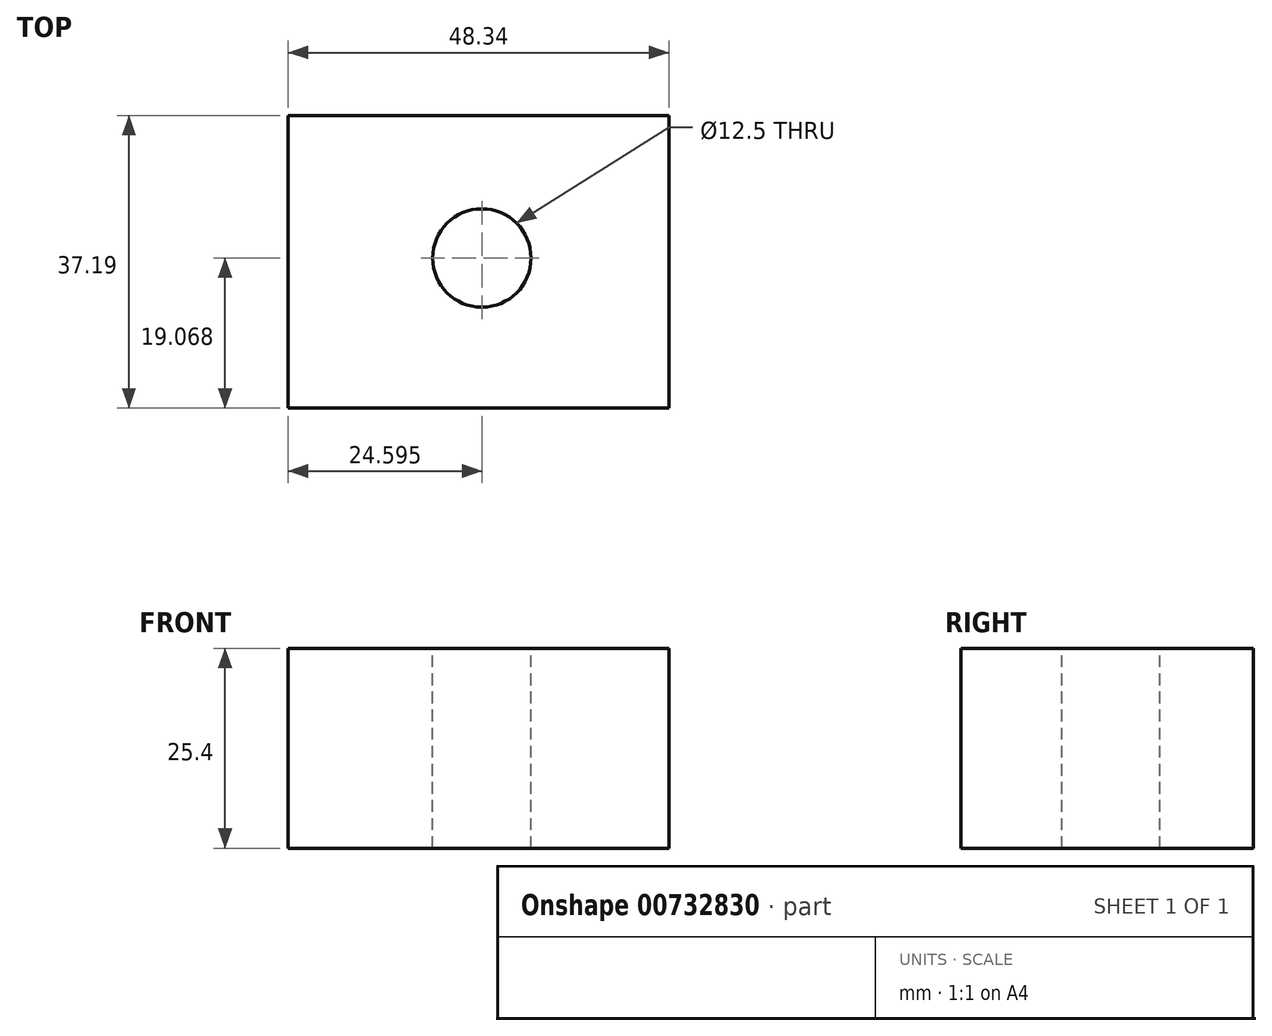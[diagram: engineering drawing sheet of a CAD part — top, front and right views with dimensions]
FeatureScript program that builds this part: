
annotation { "Feature Type Name" : "Feature", "Feature Type Description" : "" }
export const myFeature = defineFeature(function(context is Context, id is Id, definition is map)
    precondition{}
    {
        {
            var Q0;
            Q0=qCreatedBy(makeId("Top.planeOp"),FACE);
            var sketch = newSketch(context, id + "F0", { "sketchPlane" : qUnion([Q0])});
            skLineSegment(sketch, "E0.bottom", {"start": v(0, 0) * mm, "end": v(48.34, 0) * mm});
            skLineSegment(sketch, "E0.top", {"start": v(0, 37.19) * mm, "end": v(48.34, 37.19) * mm});
            skLineSegment(sketch, "E0.left", {"start": v(0, 0) * mm, "end": v(0, 37.19) * mm});
            skLineSegment(sketch, "E0.right", {"start": v(48.34, 0) * mm, "end": v(48.34, 37.19) * mm});
            skSolve(sketch);
        }
        {
            var Q0;
            Q0 = qSketchRegion(id + "F0", true);
            extrude(context, id + "F1", {"entities" : qUnion([Q0]), "depth" : 25.4 * mm, "offsetDistance" : 25.4 * mm});
        }
        {
            var Q0;
            Q0=makeQuery(id+"F1.opExtrude","CAP_FACE",FACE,{"disambiguationData":[OSD([sQuery(id+"F0.wireOp",EDGE,"E0.bottom"),sQuery(id+"F0.wireOp",EDGE,"E0.top"),sQuery(id+"F0.wireOp",EDGE,"E0.left"),sQuery(id+"F0.wireOp",EDGE,"E0.right")])],"isStart":false});
            var sketch = newSketch(context, id + "F2", { "sketchPlane" : qUnion([Q0])});
            skPoint(sketch, "E1", {"position": v(24.6, 19.07) * mm});
            skSolve(sketch);
        }
        {
            var Q0;
            Q0=sQuery(id+"F2.wireOp",VERTEX,"E1");
            var Q1;
            Q1=makeQuery(id+"F1.opExtrude","SWEPT_BODY",BODY,{"disambiguationData":[OSD([sQuery(id+"F0.wireOp",EDGE,"E0.bottom"),sQuery(id+"F0.wireOp",EDGE,"E0.top"),sQuery(id+"F0.wireOp",EDGE,"E0.left"),sQuery(id+"F0.wireOp",EDGE,"E0.right")])]});
            hole(context, id + "F3", {"style" : HoleStyle.SIMPLE, "endStyle" : HoleEndStyle.THROUGH, "standardTappedOrClearance" : lookupTablePath({ "standard" : "ISO", "engagement" : "75%", "pitch" : "1.5 mm", "size" : "M14", "type" : "Tapped" }), "standardBlindInLast" : lookupTablePath({ "standard" : "ISO", "engagement" : "75%", "pitch" : "1.5 mm", "size" : "M14", "type" : "Tapped" }), "holeDiameter" : 12.5 * mm, "majorDiameter" : 14 * mm, "showTappedDepth" : true, "isTappedThrough" : true, "tappedDepth" : 12.7 * mm, "tapClearance" : 3, "startFromSketch" : true, "locations" : qUnion([Q0]), "scope" : qUnion([Q1])});
        }
    });
